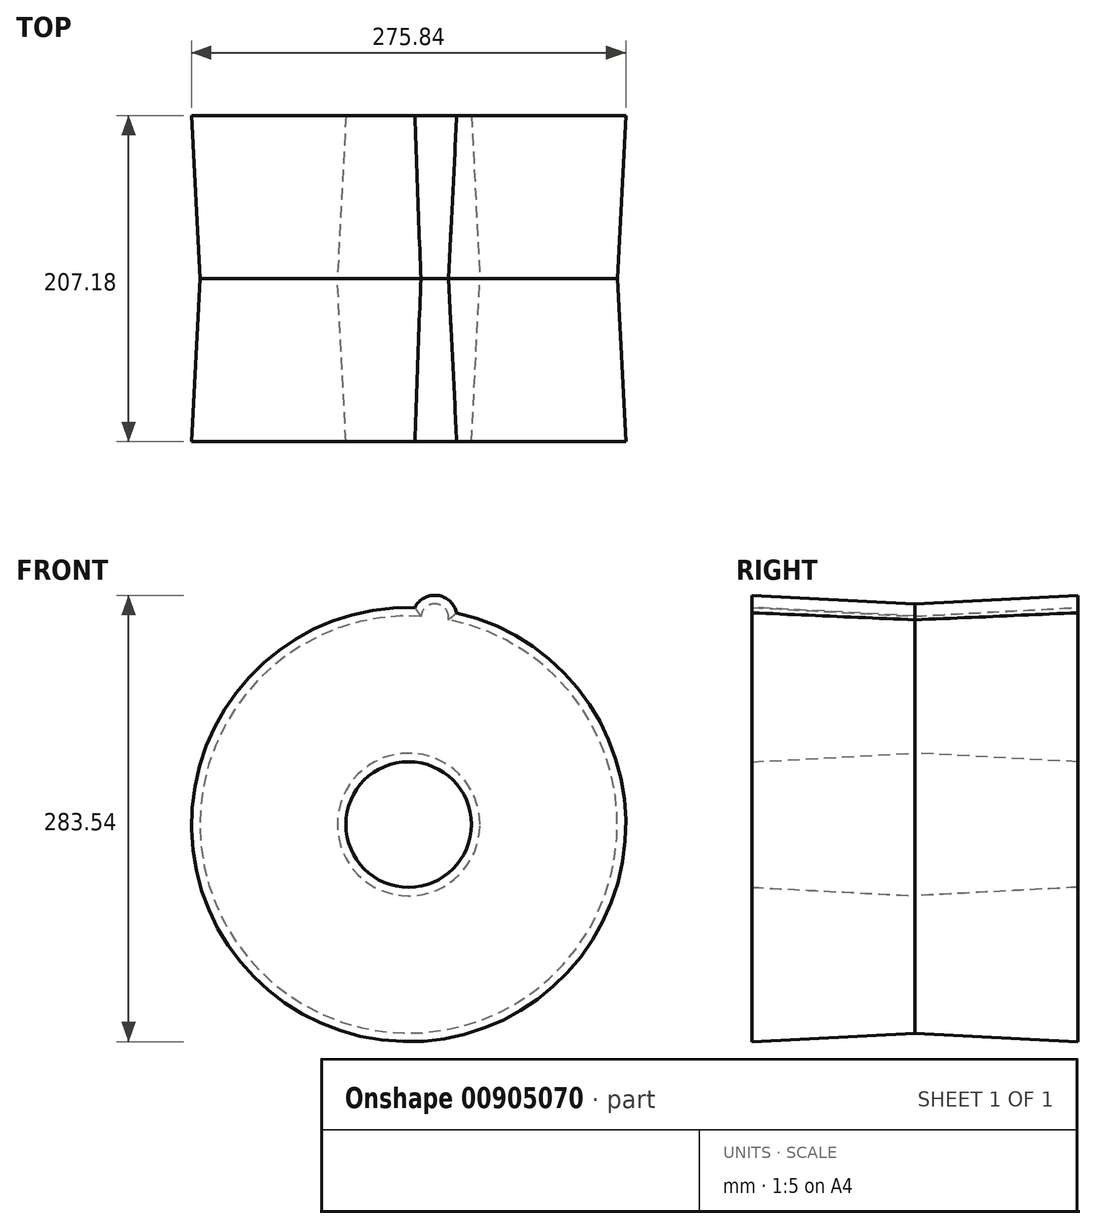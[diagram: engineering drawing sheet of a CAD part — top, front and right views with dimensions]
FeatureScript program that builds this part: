
annotation { "Feature Type Name" : "Feature", "Feature Type Description" : "" }
export const myFeature = defineFeature(function(context is Context, id is Id, definition is map)
    precondition{}
    {
        {
            var Q0;
            Q0=qCreatedBy(makeId("Front.planeOp"),FACE);
            var sketch = newSketch(context, id + "F0", { "sketchPlane" : qUnion([Q0])});
            skCircle(sketch, "E0", {"center": v(0, 8.32) * mm, "radius": 45.28 * mm});
            skCircle(sketch, "E1", {"center": v(0, 8.32) * mm, "radius": 132.5 * mm});
            skCircle(sketch, "E2", {"center": v(16.6, 139.77) * mm, "radius": 8.74 * mm});
            skSolve(sketch);
        }
        {
            var Q0;
            Q0 = qSketchRegion(id + "F0", true);
            extrude(context, id + "F1", {"entities" : qUnion([Q0]), "endBound" : BoundingType.SYMMETRIC, "depth" : 207.2 * mm, "offsetDistance" : 25 * mm, "hasDraft" : true, "draftAngle" : 3 * degree});
        }
    });
